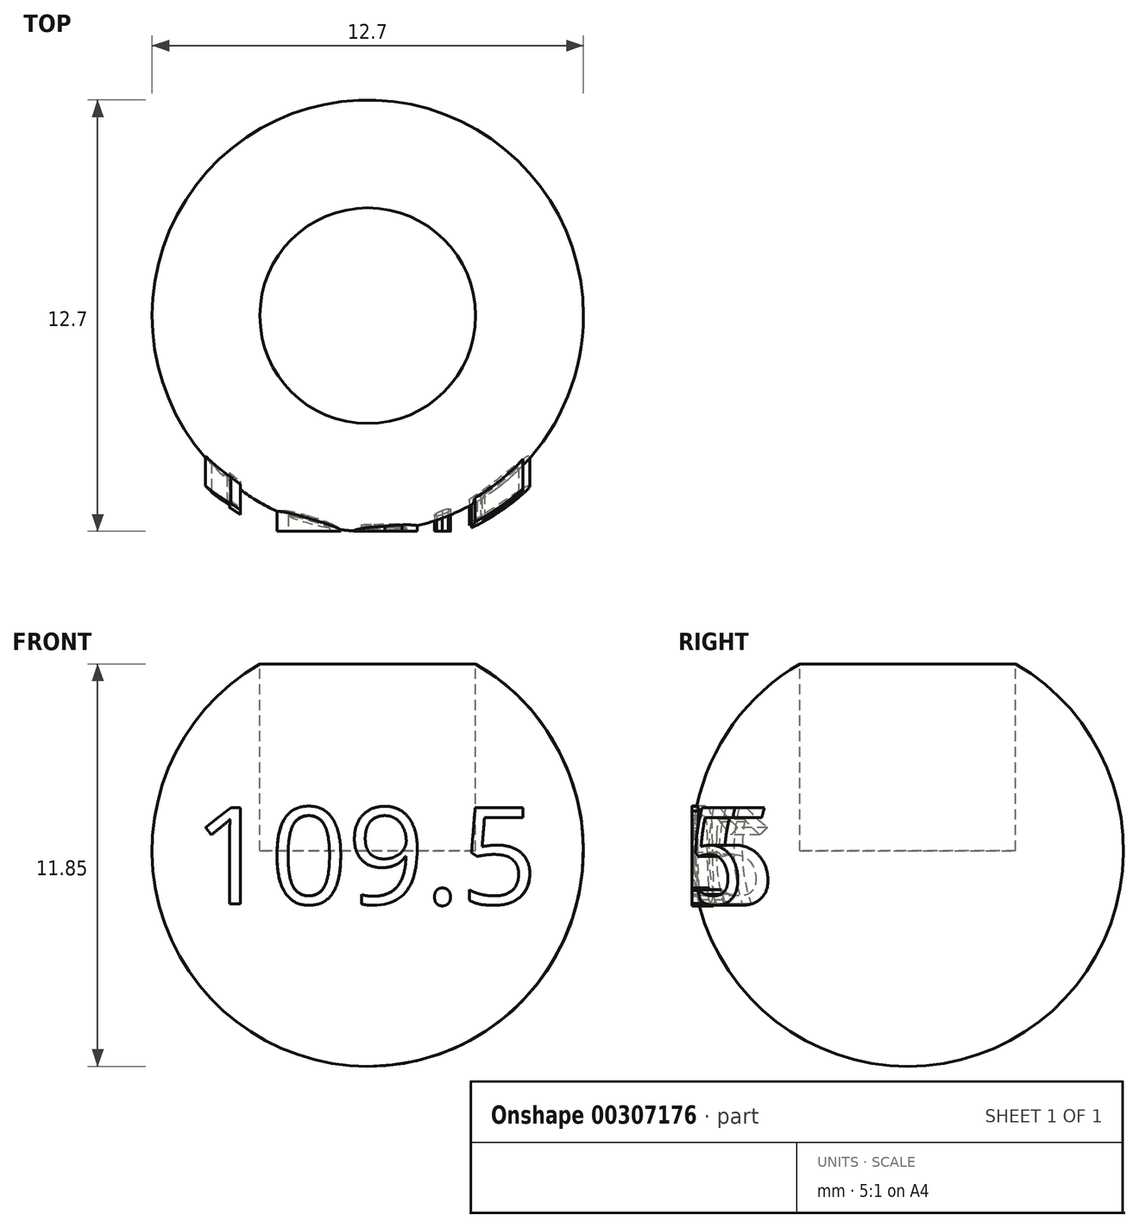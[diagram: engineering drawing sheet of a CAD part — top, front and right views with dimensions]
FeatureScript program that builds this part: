
annotation { "Feature Type Name" : "Feature", "Feature Type Description" : "" }
export const myFeature = defineFeature(function(context is Context, id is Id, definition is map)
    precondition{}
    {
        {
            var Q0;
            Q0=qCreatedBy(makeId("Front.planeOp"),FACE);
            var sketch = newSketch(context, id + "F0", { "sketchPlane" : qUnion([Q0])});
            skArc(sketch, "E0", {"start": v(0, 6.35) * mm, "mid": v(-6.35, 0) * mm, "end": v(0, -6.35) * mm});
            skLineSegment(sketch, "E1", {"start": v(0, 6.35) * mm, "end": v(0, -6.35) * mm});
            skSolve(sketch);
        }
        {
            var Q0;
            Q0=qCreatedBy(makeId("Top.planeOp"),FACE);
            var sketch = newSketch(context, id + "F1", { "sketchPlane" : qUnion([Q0])});
            skCircle(sketch, "E2", {"center": v(0, 0) * mm, "radius": 6.35 * mm});
            skSolve(sketch);
        }
        {
            var Q0;
            Q0=makeQuery(id+"F0.imprint","IMPRINT",FACE,{"disambiguationData":[TD([[makeQuery(id+"F0.imprint","IMPRINT",EDGE,{"derivedFrom":sQuery(id+"F0.wireOp",EDGE,"E0")}),1.0]])]});
            var Q1;
            Q1=sQuery(id+"F1.wireOp",EDGE,"E2");
            revolve(context, id + "F2", {"entities" : qUnion([Q0]), "axis" : qUnion([Q1]), "revolveType" : RevolveType.FULL});
        }
        {
            var Q0;
            Q0=qCreatedBy(makeId("Top.planeOp"),FACE);
            cPlane(context, id + "F3", {"entities" : qUnion([Q0]), "cplaneType" : CPlaneType.OFFSET, "offset" : 6.35 * mm, "width" : 152.4 * mm, "height" : 152.4 * mm});
        }
        {
            var Q0;
            Q0=qCreatedBy(id+"F3.planeOp",FACE);
            var sketch = newSketch(context, id + "F4", { "sketchPlane" : qUnion([Q0])});
            skCircle(sketch, "E3", {"center": v(0, 0) * mm, "radius": 3.18 * mm});
            skSolve(sketch);
        }
        {
            var Q0;
            Q0 = qSketchRegion(id + "F4", true);
            extrude(context, id + "F5", {"entities" : qUnion([Q0]), "operationType" : NewBodyOperationType.REMOVE, "oppositeDirection" : true, "depth" : 6.35 * mm});
        }
        {
            var Q0;
            Q0=makeQuery(id+"F5.boolean.opBoolean","COPY",FACE,{"derivedFrom":makeQuery(id+"F5.opExtrude","CAP_FACE",FACE,{"disambiguationData":[OSD([sQuery(id+"F4.wireOp",EDGE,"E3")])],"isStart":false})});
            extrude(context, id + "F6", {"entities" : qUnion([Q0]), "depth" : 76.2 * mm});
        }
        {
            var Q0;
            Q0=qCreatedBy(makeId("Front.planeOp"),FACE);
            var sketch = newSketch(context, id + "F7", { "sketchPlane" : qUnion([Q0])});
            skLineSegment(sketch, "E4", {"start": v(0, 0) * mm, "end": v(26.95, 0) * mm, "construction": true});
            skLineSegment(sketch, "E5", {"start": v(0, 0) * mm, "end": v(0, -26.65) * mm, "construction": true});
            skSolve(sketch);
        }
        {
            var Q0;
            Q0=makeQuery(id+"F6.opExtrude","SWEPT_BODY",BODY,{"disambiguationData":[OSD([sQuery(id+"F4.wireOp",EDGE,"E3")])]});
            var Q1;
            Q1=sQuery(id+"F7.wireOp",EDGE,"E4");
            transform(context, id + "F8", {"entities" : qUnion([Q0]), "transformType" : TransformType.ROTATION, "transformAxis" : qUnion([Q1]), "angle" : 109.5 * degree, "makeCopy" : true});
        }
        {
            var Q0;
            Q0=makeQuery(id+"F8.opPattern","COPY",BODY,{"derivedFrom":makeQuery(id+"F6.opExtrude","SWEPT_BODY",BODY,{"disambiguationData":[OSD([sQuery(id+"F4.wireOp",EDGE,"E3")])]}),"instanceName":"1"});
            var Q1;
            Q1=sQuery(id+"F7.wireOp",EDGE,"E5");
            transform(context, id + "F9", {"entities" : qUnion([Q0]), "transformType" : TransformType.ROTATION, "transformAxis" : qUnion([Q1]), "angle" : 120 * degree, "makeCopy" : true});
        }
        {
            var Q0;
            Q0=makeQuery(id+"F9.opPattern","COPY",BODY,{"derivedFrom":makeQuery(id+"F8.opPattern","COPY",BODY,{"derivedFrom":makeQuery(id+"F6.opExtrude","SWEPT_BODY",BODY,{"disambiguationData":[OSD([sQuery(id+"F4.wireOp",EDGE,"E3")])]}),"instanceName":"1"}),"instanceName":"1"});
            var Q1;
            Q1=sQuery(id+"F7.wireOp",EDGE,"E5");
            transform(context, id + "F10", {"entities" : qUnion([Q0]), "transformType" : TransformType.ROTATION, "transformAxis" : qUnion([Q1]), "angle" : 120 * degree, "makeCopy" : true});
        }
        {
            var Q0;
            Q0=qCreatedBy(makeId("Front.planeOp"),FACE);
            cPlane(context, id + "F11", {"entities" : qUnion([Q0]), "cplaneType" : CPlaneType.OFFSET, "offset" : 6.35 * mm, "width" : 152.4 * mm, "height" : 152.4 * mm});
        }
        {
            var Q0;
            Q0=makeQuery(id+"F8.opPattern","COPY",BODY,{"derivedFrom":makeQuery(id+"F6.opExtrude","SWEPT_BODY",BODY,{"disambiguationData":[OSD([sQuery(id+"F4.wireOp",EDGE,"E3")])]}),"instanceName":"1"});
            var Q1;
            Q1=makeQuery(id+"F10.opPattern","COPY",BODY,{"derivedFrom":makeQuery(id+"F9.opPattern","COPY",BODY,{"derivedFrom":makeQuery(id+"F8.opPattern","COPY",BODY,{"derivedFrom":makeQuery(id+"F6.opExtrude","SWEPT_BODY",BODY,{"disambiguationData":[OSD([sQuery(id+"F4.wireOp",EDGE,"E3")])]}),"instanceName":"1"}),"instanceName":"1"}),"instanceName":"1"});
            var Q2;
            Q2=makeQuery(id+"F9.opPattern","COPY",BODY,{"derivedFrom":makeQuery(id+"F8.opPattern","COPY",BODY,{"derivedFrom":makeQuery(id+"F6.opExtrude","SWEPT_BODY",BODY,{"disambiguationData":[OSD([sQuery(id+"F4.wireOp",EDGE,"E3")])]}),"instanceName":"1"}),"instanceName":"1"});
            deleteBodies(context, id + "F12", {"entities" : qUnion([Q0, Q1, Q2])});
        }
        {
            var Q0;
            Q0=qCreatedBy(id+"F11.planeOp",FACE);
            var sketch = newSketch(context, id + "F13", { "sketchPlane" : qUnion([Q0])});
            skText(sketch, "E6", { "text": "109.5", "fontName": "OpenSans-Regular.ttf"});
            const initialGuessF13  = {"E6": [-0.00514, -0.00157, 1, 0, 0.00286]};
            skSetInitialGuess(sketch, initialGuessF13);
            skSolve(sketch);
        }
        {
            var Q0;
            Q0 = qSketchRegion(id + "F13", true);
            extrude(context, id + "F14", {"entities" : qUnion([Q0]), "operationType" : NewBodyOperationType.ADD, "oppositeDirection" : true, "depth" : 2.54 * mm});
        }
        {
            var Q0;
            Q0=qCreatedBy(makeId("Front.planeOp"),FACE);
            var sketch = newSketch(context, id + "F15", { "sketchPlane" : qUnion([Q0])});
            skArc(sketch, "E7", {"start": v(0, 6.96) * mm, "mid": v(-6.96, 0) * mm, "end": v(0, -6.96) * mm});
            skArc(sketch, "E8", {"start": v(0, 11.4) * mm, "mid": v(-11.4, 0) * mm, "end": v(0, -11.4) * mm});
            skLineSegment(sketch, "E9", {"start": v(0, 11.4) * mm, "end": v(0, 6.96) * mm});
            skLineSegment(sketch, "E10", {"start": v(0, -6.96) * mm, "end": v(0, -11.4) * mm});
            skLineSegment(sketch, "E11", {"start": v(0, 11.4) * mm, "end": v(0, 0) * mm, "construction": true});
            skSolve(sketch);
        }
        {
            var Q0;
            Q0=makeQuery(id+"F15.imprint","IMPRINT",FACE,{"disambiguationData":[TD([[makeQuery(id+"F15.imprint","IMPRINT",EDGE,{"derivedFrom":sQuery(id+"F15.wireOp",EDGE,"E7")}),-1.0]])]});
            var Q1;
            Q1=sQuery(id+"F15.wireOp",EDGE,"E11");
            revolve(context, id + "F16", {"operationType" : NewBodyOperationType.REMOVE, "entities" : qUnion([Q0]), "axis" : qUnion([Q1]), "revolveType" : RevolveType.FULL, "oppositeDirection" : true});
        }
        {
            var Q0;
            Q0=makeQuery(id+"F6.opExtrude","SWEPT_BODY",BODY,{"disambiguationData":[OSD([sQuery(id+"F4.wireOp",EDGE,"E3")])]});
            var Q1;
            Q1=sQuery(id+"F7.wireOp",EDGE,"E4");
            transform(context, id + "F17", {"entities" : qUnion([Q0]), "transformType" : TransformType.ROTATION, "transformAxis" : qUnion([Q1]), "angle" : 109.5 * degree, "oppositeDirection" : true, "makeCopy" : true});
        }
        {
            var Q0;
            Q0=makeQuery(id+"F6.opExtrude","SWEPT_BODY",BODY,{"disambiguationData":[OSD([sQuery(id+"F4.wireOp",EDGE,"E3")])]});
            deleteBodies(context, id + "F18", {"entities" : qUnion([Q0])});
        }
        {
            var Q0;
            Q0=makeQuery(id+"F17.opPattern","COPY",BODY,{"derivedFrom":makeQuery(id+"F6.opExtrude","SWEPT_BODY",BODY,{"disambiguationData":[OSD([sQuery(id+"F4.wireOp",EDGE,"E3")])]}),"instanceName":"1"});
            deleteBodies(context, id + "F19", {"entities" : qUnion([Q0])});
        }
        {
            var Q0;
            Q0=qCreatedBy(makeId("Top.planeOp"),FACE);
            cPlane(context, id + "F20", {"entities" : qUnion([Q0]), "cplaneType" : CPlaneType.OFFSET, "offset" : 3.17 * mm, "width" : 152.4 * mm, "height" : 152.4 * mm});
        }
        {
            var Q0;
            Q0=qCreatedBy(id+"F20.planeOp",FACE);
            var sketch = newSketch(context, id + "F21", { "sketchPlane" : qUnion([Q0])});
            skCircle(sketch, "E12", {"center": v(0, 0) * mm, "radius": 3.18 * mm});
            skSolve(sketch);
        }
        {
            var Q0;
            Q0 = qSketchRegion(id + "F21", true);
            extrude(context, id + "F22", {"entities" : qUnion([Q0]), "depth" : 76.2 * mm});
        }
        {
            var Q0;
            Q0=makeQuery(id+"F22.opExtrude","SWEPT_BODY",BODY,{"disambiguationData":[OSD([sQuery(id+"F21.wireOp",EDGE,"E12")])]});
            var Q1;
            Q1=sQuery(id+"F7.wireOp",EDGE,"E4");
            transform(context, id + "F23", {"entities" : qUnion([Q0]), "transformType" : TransformType.ROTATION, "transformAxis" : qUnion([Q1]), "angle" : 109.5 * degree, "oppositeDirection" : true, "makeCopy" : true});
        }
        {
            var Q0;
            Q0=makeQuery(id+"F22.opExtrude","SWEPT_BODY",BODY,{"disambiguationData":[OSD([sQuery(id+"F21.wireOp",EDGE,"E12")])]});
            deleteBodies(context, id + "F24", {"entities" : qUnion([Q0])});
        }
        {
            var Q0;
            Q0=makeQuery(id+"F23.opPattern","COPY",BODY,{"derivedFrom":makeQuery(id+"F22.opExtrude","SWEPT_BODY",BODY,{"disambiguationData":[OSD([sQuery(id+"F21.wireOp",EDGE,"E12")])]}),"instanceName":"1"});
            deleteBodies(context, id + "F25", {"entities" : qUnion([Q0])});
        }
    });
